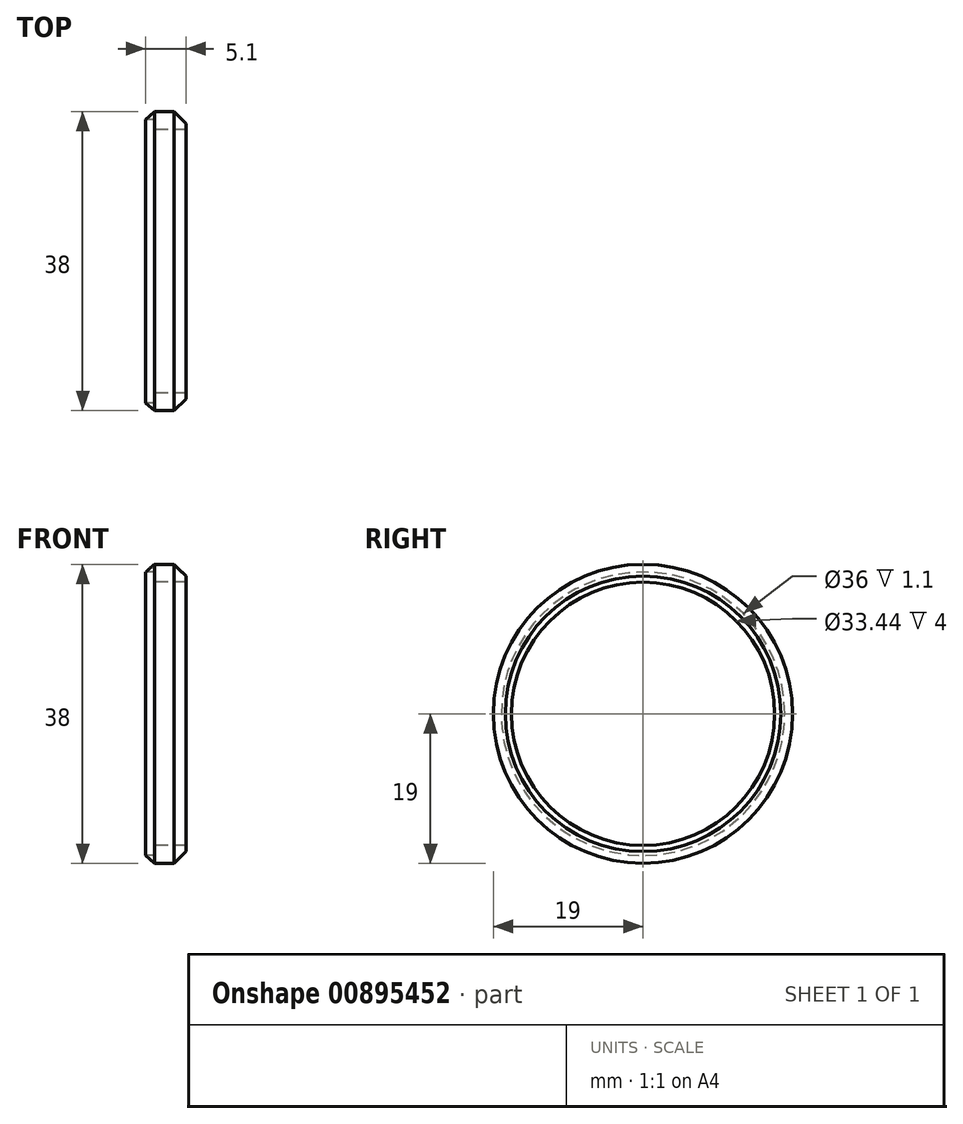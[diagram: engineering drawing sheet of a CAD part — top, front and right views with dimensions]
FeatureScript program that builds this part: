
annotation { "Feature Type Name" : "Feature", "Feature Type Description" : "" }
export const myFeature = defineFeature(function(context is Context, id is Id, definition is map)
    precondition{}
    {
        {
            var Q0;
            Q0=qCreatedBy(makeId("Front.planeOp"),FACE);
            var sketch = newSketch(context, id + "F0", { "sketchPlane" : qUnion([Q0])});
            skLineSegment(sketch, "E0", {"start": v(-2.5, 19) * mm, "end": v(0, 19) * mm});
            skLineSegment(sketch, "E1", {"start": v(0, 19) * mm, "end": v(1.5, 17.5) * mm});
            skLineSegment(sketch, "E2", {"start": v(1.5, 17.5) * mm, "end": v(1.5, 16.72) * mm});
            skLineSegment(sketch, "E3", {"start": v(1.5, 16.72) * mm, "end": v(-2.5, 16.72) * mm});
            skLineSegment(sketch, "E4", {"start": v(-2.5, 16.72) * mm, "end": v(-2.5, 18) * mm});
            skLineSegment(sketch, "E5", {"start": v(-2.5, 18) * mm, "end": v(-3.6, 18) * mm});
            skLineSegment(sketch, "E6", {"start": v(-3.6, 18) * mm, "end": v(-2.5, 19) * mm});
            skLineSegment(sketch, "E7", {"start": v(0, 0) * mm, "end": v(3.52, 0) * mm});
            skLineSegment(sketch, "E8", {"start": v(3.12, 20.94) * mm, "end": v(1.5, 17.5) * mm});
            skFitSpline(sketch, "E9", {"points": [v(-1.64, 19) * mm, v(1.9, 23.45) * mm], "startDerivative": vector(2.62, 4.4) * mm, "endDerivative": vector(5.7, 2.51) * mm});
            skFitSpline(sketch, "E10", {"points": [v(1.9, 23.45) * mm, v(3.2, 23.45) * mm], "startDerivative": vector(1.51, 0) * mm, "endDerivative": vector(1.51, 0) * mm});
            skFitSpline(sketch, "E11", {"points": [v(3.2, 23.45) * mm, v(3.12, 20.94) * mm], "startDerivative": vector(-0.3, -2.53) * mm, "endDerivative": vector(-0.3, -2.53) * mm});
            skSolve(sketch);
        }
        {
            var Q0;
            Q0=makeQuery(id+"F0.imprint","IMPRINT",FACE,{"disambiguationData":[TD([[makeQuery(id+"F0.imprint","IMPRINT",EDGE,{"derivedFrom":sQuery(id+"F0.wireOp",EDGE,"E0")}),-1.0]])]});
            var Q1;
            Q1=sQuery(id+"F0.wireOp",EDGE,"E7");
            revolve(context, id + "F1", {"surfaceOperationType" : NewSurfaceOperationType.NEW, "entities" : qUnion([Q0]), "axis" : qUnion([Q1]), "revolveType" : RevolveType.FULL});
        }
    });
